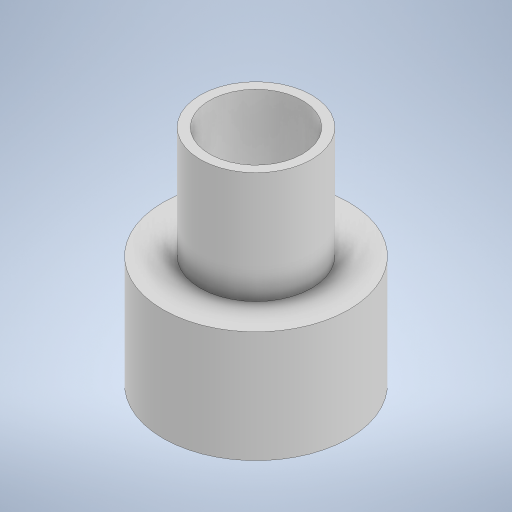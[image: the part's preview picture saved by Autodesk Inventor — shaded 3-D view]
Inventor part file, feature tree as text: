
AUTODESK INVENTOR PART (.ipt)
format: ipt  version: 2024 (Build 280153000, 153)  size: 252,928 bytes
history: native  units: in
note: dims shown in document units (in); Inventor stores cm internally (conversion verified against a paired STEP export)
features: sketch x4, extrude x3
ambient origin geometry x8: Origin, YZ Plane, XZ Plane, XY Plane, X Axis, Y Axis, Z Axis, Center Point
bodies: Body1 (feature_tree)
feature tree (7):
  extrude  "Extrusion21"  Depth=1.1811in TaperAngle=0.0deg
  extrude  "Extrusion22"  Depth=1.1811in TaperAngle=0.0deg
  extrude  "Extrusion23"  Depth=1.1811in TaperAngle=0.0deg
  sketch  "Sketch33"  dims[d42=0.0197in d43=0.0344in d44=0.0197in d45=0.0344in d46=0.0in d47=0.0in d48=0.0in d49=0.0in d50=0.0in d51=0.0in d52=0.0in d53=0.0in d55=0.0197in d56=0.0344in d57=0.0197in d58=0.0344in d60=0.0197in d61=0.0344in d62=0.0197in d63=0.0344in d72=0.0197in d73=0.0344in d74=0.0197in d75=0.0344in d126=0.0197in d127=0.0344in]
  sketch  "Sketch30"  dims[d117=1.9685in d118=1.1811in d119=0.0in]
  sketch  "Sketch31"  dims[d120=1.1811in d121=1.1811in d122=0.0in]
  sketch  "Sketch32"  dims[d123=0.9843in d124=1.1811in d125=0.0in]
